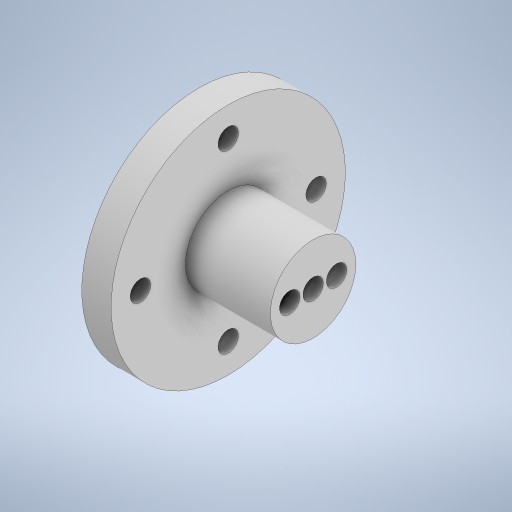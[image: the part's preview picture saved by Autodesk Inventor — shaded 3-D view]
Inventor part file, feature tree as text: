
AUTODESK INVENTOR PART (.ipt)
format: ipt  version: 2023 (Build 270158000, 158)  size: 278,528 bytes
history: native  units: mm
features: extrude x2, sketch x2
ambient origin geometry x8: Origin, YZ Plane, XZ Plane, XY Plane, X Axis, Y Axis, Z Axis, Center Point
bodies: Solid1 (feature_tree)
feature tree (4):
  extrude  "Extrusion1"  Depth=3.5mm
  extrude  "Extrusion5"  Depth=14.5mm
  sketch  "Sketch1"  dims[d0=30.0mm d1=3.5mm]
  sketch  "Sketch5"  dims[d2=40.0mm d4=360.0deg d6=3.5mm d7=40.0mm d8=5.0mm d9=0.0mm d38=8.0mm d39=3.5mm d40=20.0mm d42=360.0deg d44=14.6mm d45=14.5mm d46=0.0mm]
